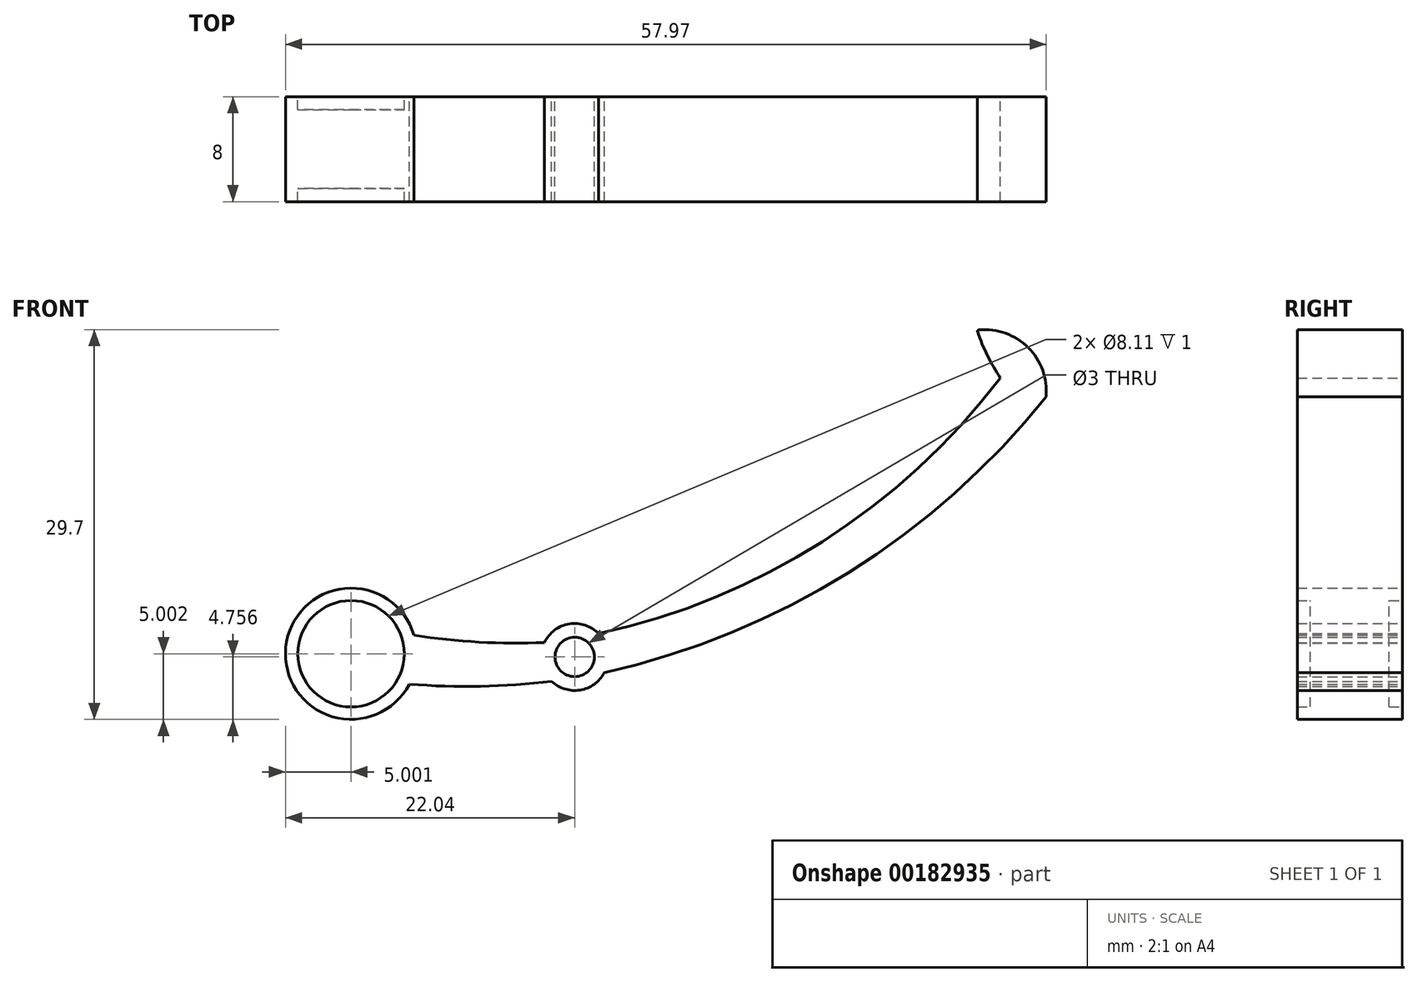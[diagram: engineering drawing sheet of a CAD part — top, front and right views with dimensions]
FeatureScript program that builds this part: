
annotation { "Feature Type Name" : "Feature", "Feature Type Description" : "" }
export const myFeature = defineFeature(function(context is Context, id is Id, definition is map)
    precondition{}
    {
        {
            var Q0;
            Q0=qCreatedBy(makeId("Front.planeOp"),FACE);
            var sketch = newSketch(context, id + "F0", { "sketchPlane" : qUnion([Q0])});
            skCircle(sketch, "E0", {"center": v(0, -69.95) * mm, "radius": 1.5 * mm});
            skPoint(sketch, "E1.visualSharp", {"position": v(32.48, -48.77) * mm});
            skArc(sketch, "E2", {"start": v(35.91, -50.13) * mm, "mid": v(34.55, -46.38) * mm, "end": v(30.79, -45.03) * mm});
            skArc(sketch, "E3", {"start": v(30.7, -45.18) * mm, "mid": v(31.45, -47) * mm, "end": v(32.43, -48.7) * mm});
            skArc(sketch, "E4.filletArc", {"start": v(30.79, -45.03) * mm, "mid": v(30.7, -45.08) * mm, "end": v(30.7, -45.18) * mm});
            skArc(sketch, "E5", {"start": v(-12.24, -68.3) * mm, "mid": v(-7.29, -68.82) * mm, "end": v(-2.3, -68.86) * mm});
            skArc(sketch, "E6", {"start": v(-12.6, -72.02) * mm, "mid": v(-7.18, -72.19) * mm, "end": v(-1.76, -71.8) * mm});
            skArc(sketch, "E7", {"start": v(1.83, -68.18) * mm, "mid": v(-0.41, -67.44) * mm, "end": v(-2.3, -68.86) * mm});
            skArc(sketch, "E8.trimOffspring", {"start": v(1.83, -68.18) * mm, "mid": v(18.87, -61.17) * mm, "end": v(32.43, -48.7) * mm});
            skArc(sketch, "E9.trimOffspring", {"start": v(2.26, -71.15) * mm, "mid": v(20.88, -63.52) * mm, "end": v(35.91, -50.13) * mm});
            skArc(sketch, "E10.trimOffspring", {"start": v(-1.76, -71.8) * mm, "mid": v(0.41, -72.47) * mm, "end": v(2.26, -71.15) * mm});
            skPoint(sketch, "E11.orphan", {"position": v(-17.75, -71.35) * mm});
            skArc(sketch, "E12", {"start": v(-12.24, -68.3) * mm, "mid": v(-22.02, -69.23) * mm, "end": v(-12.6, -72.02) * mm});
            skPoint(sketch, "E13.orphan", {"position": v(-8.68, -68.72) * mm});
            skCircle(sketch, "E14", {"center": v(-17.04, -69.7) * mm, "radius": 4.05 * mm});
            skSolve(sketch);
        }
        {
            var Q0;
            {var subQ0=sQuery(id+"F0.wireOp",EDGE,"E12");Q0=makeQuery(id+"F0.imprint","IMPRINT",FACE,{"disambiguationData":[TD([[makeQuery(id+"F0.imprint","IMPRINT",EDGE,{"derivedFrom":subQ0}),-1.0]])]});}
            var Q1;
            Q1=makeQuery(id+"F0.imprint","IMPRINT",FACE,{"disambiguationData":[TD([[makeQuery(id+"F0.imprint","IMPRINT",EDGE,{"derivedFrom":sQuery(id+"F0.wireOp",EDGE,"E0")}),-1.0]])]});
            extrude(context, id + "F1", {"entities" : qUnion([Q0, Q1]), "endBound" : BoundingType.SYMMETRIC, "depth" : 5 * mm});
        }
        {
            var Q0;
            {var subQ0=sQuery(id+"F0.wireOp",EDGE,"E12");Q0=makeQuery(id+"F0.imprint","IMPRINT",FACE,{"disambiguationData":[TD([[makeQuery(id+"F0.imprint","IMPRINT",EDGE,{"derivedFrom":subQ0}),1.0]])]});}
            extrude(context, id + "F2", {"entities" : qUnion([Q0]), "operationType" : NewBodyOperationType.ADD, "endBound" : BoundingType.SYMMETRIC, "depth" : 8 * mm});
        }
        {
            var Q0;
            Q0=makeQuery(id+"F0.imprint","IMPRINT",FACE,{"disambiguationData":[TD([[makeQuery(id+"F0.imprint","IMPRINT",EDGE,{"derivedFrom":sQuery(id+"F0.wireOp",EDGE,"E14")}),1.0]])]});
            extrude(context, id + "F3", {"entities" : qUnion([Q0]), "operationType" : NewBodyOperationType.ADD, "endBound" : BoundingType.SYMMETRIC, "depth" : 6 * mm});
        }
    });
